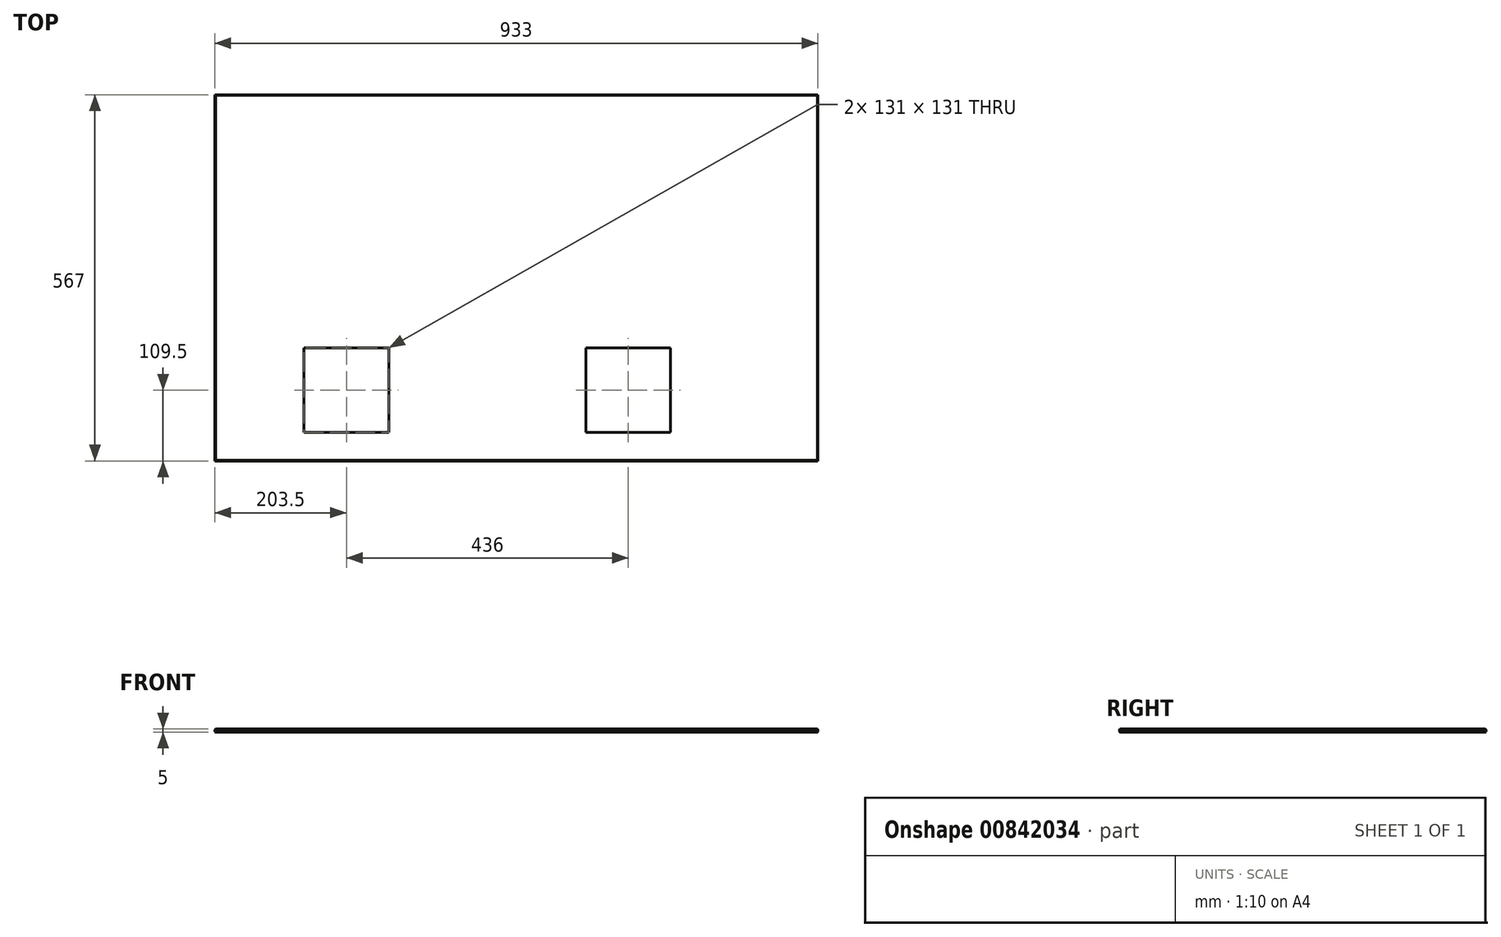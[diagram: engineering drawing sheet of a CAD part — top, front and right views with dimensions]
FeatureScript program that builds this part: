
annotation { "Feature Type Name" : "Feature", "Feature Type Description" : "" }
export const myFeature = defineFeature(function(context is Context, id is Id, definition is map)
    precondition{}
    {
        {
            var Q0;
            Q0=qCreatedBy(makeId("Top.planeOp"),FACE);
            var sketch = newSketch(context, id + "F0", { "sketchPlane" : qUnion([Q0])});
            skLineSegment(sketch, "E0.bottom", {"start": v(-466.5, 283.5) * mm, "end": v(466.5, 283.5) * mm});
            skLineSegment(sketch, "E0.top", {"start": v(-466.5, -283.5) * mm, "end": v(466.5, -283.5) * mm});
            skLineSegment(sketch, "E0.left", {"start": v(-466.5, 283.5) * mm, "end": v(-466.5, -283.5) * mm});
            skLineSegment(sketch, "E0.right", {"start": v(466.5, 283.5) * mm, "end": v(466.5, -283.5) * mm});
            skPoint(sketch, "E0.middle", {"position": v(0, 0) * mm});
            skSolve(sketch);
        }
        {
            var Q0;
            Q0=makeQuery(id+"F0.imprint","IMPRINT",FACE,{"disambiguationData":[TD([[makeQuery(id+"F0.imprint","IMPRINT",EDGE,{"derivedFrom":sQuery(id+"F0.wireOp",EDGE,"E0.bottom")}),-1.0]])]});
            extrude(context, id + "F1", {"entities" : qUnion([Q0]), "endBound" : BoundingType.SYMMETRIC, "depth" : 5 * mm, "offsetDistance" : 25 * mm});
        }
        {
            var Q0;
            Q0=makeQuery(id+"F1.opExtrude","CAP_FACE",FACE,{"disambiguationData":[OSD([sQuery(id+"F0.wireOp",EDGE,"E0.bottom"),sQuery(id+"F0.wireOp",EDGE,"E0.top"),sQuery(id+"F0.wireOp",EDGE,"E0.left"),sQuery(id+"F0.wireOp",EDGE,"E0.right")])],"isStart":false});
            var sketch = newSketch(context, id + "F2", { "sketchPlane" : qUnion([Q0])});
            skLineSegment(sketch, "E1.bottom", {"start": v(-328.5, -108.5) * mm, "end": v(-197.5, -108.5) * mm});
            skLineSegment(sketch, "E1.top", {"start": v(-328.5, -239.5) * mm, "end": v(-197.5, -239.5) * mm});
            skLineSegment(sketch, "E1.left", {"start": v(-328.5, -108.5) * mm, "end": v(-328.5, -239.5) * mm});
            skLineSegment(sketch, "E1.right", {"start": v(-197.5, -108.5) * mm, "end": v(-197.5, -239.5) * mm});
            skSolve(sketch);
        }
        {
            var Q0;
            Q0=makeQuery(id+"F2.imprint","IMPRINT",FACE,{"disambiguationData":[TD([[makeQuery(id+"F2.imprint","IMPRINT",EDGE,{"derivedFrom":sQuery(id+"F2.wireOp",EDGE,"E1.bottom")}),-1.0]])]});
            extrude(context, id + "F3", {"entities" : qUnion([Q0]), "operationType" : NewBodyOperationType.REMOVE, "endBound" : BoundingType.THROUGH_ALL, "oppositeDirection" : true, "depth" : 25 * mm, "offsetDistance" : 25 * mm});
        }
        {
            var Q0;
            Q0=makeQuery(id+"F2.imprint","IMPRINT",FACE,{"disambiguationData":[TD([[makeQuery(id+"F2.imprint","IMPRINT",EDGE,{"derivedFrom":sQuery(id+"F2.wireOp",EDGE,"E1.bottom")}),1.0]])]});
            var sketch = newSketch(context, id + "F4", { "sketchPlane" : qUnion([Q0])});
            skLineSegment(sketch, "E2.bottom", {"start": v(107.5, -108.5) * mm, "end": v(238.5, -108.5) * mm});
            skLineSegment(sketch, "E2.top", {"start": v(107.5, -239.5) * mm, "end": v(238.5, -239.5) * mm});
            skLineSegment(sketch, "E2.left", {"start": v(107.5, -108.5) * mm, "end": v(107.5, -239.5) * mm});
            skLineSegment(sketch, "E2.right", {"start": v(238.5, -108.5) * mm, "end": v(238.5, -239.5) * mm});
            skSolve(sketch);
        }
        {
            var Q0;
            Q0=makeQuery(id+"F4.imprint","IMPRINT",FACE,{"disambiguationData":[TD([[makeQuery(id+"F4.imprint","IMPRINT",EDGE,{"derivedFrom":sQuery(id+"F4.wireOp",EDGE,"E2.bottom")}),-1.0]])]});
            extrude(context, id + "F5", {"entities" : qUnion([Q0]), "operationType" : NewBodyOperationType.REMOVE, "endBound" : BoundingType.THROUGH_ALL, "oppositeDirection" : true, "depth" : 25 * mm, "offsetDistance" : 25 * mm});
        }
        {
            var Q0;
            Q0=makeQuery(id+"F1.opExtrude","CAP_EDGE",EDGE,{"disambiguationData":[OSD([sQuery(id+"F0.wireOp",EDGE,"E0.left")])],"isStart":false});
            var Q1;
            Q1=makeQuery(id+"F1.opExtrude","CAP_EDGE",EDGE,{"disambiguationData":[OSD([sQuery(id+"F0.wireOp",EDGE,"E0.left")])],"isStart":true});
            var Q2;
            Q2=makeQuery(id+"F1.opExtrude","CAP_EDGE",EDGE,{"disambiguationData":[OSD([sQuery(id+"F0.wireOp",EDGE,"E0.top")])],"isStart":true});
            var Q3;
            Q3=makeQuery(id+"F1.opExtrude","CAP_EDGE",EDGE,{"disambiguationData":[OSD([sQuery(id+"F0.wireOp",EDGE,"E0.top")])],"isStart":false});
            var Q4;
            Q4=makeQuery(id+"F1.opExtrude","CAP_EDGE",EDGE,{"disambiguationData":[OSD([sQuery(id+"F0.wireOp",EDGE,"E0.right")])],"isStart":true});
            var Q5;
            Q5=makeQuery(id+"F1.opExtrude","CAP_EDGE",EDGE,{"disambiguationData":[OSD([sQuery(id+"F0.wireOp",EDGE,"E0.right")])],"isStart":false});
            var Q6;
            Q6=makeQuery(id+"F1.opExtrude","CAP_EDGE",EDGE,{"disambiguationData":[OSD([sQuery(id+"F0.wireOp",EDGE,"E0.bottom")])],"isStart":false});
            var Q7;
            Q7=makeQuery(id+"F1.opExtrude","CAP_EDGE",EDGE,{"disambiguationData":[OSD([sQuery(id+"F0.wireOp",EDGE,"E0.bottom")])],"isStart":true});
            chamfer(context, id + "F6", {"entities" : qUnion([Q0, Q1, Q2, Q3, Q4, Q5, Q6, Q7]), "width" : 1 * mm, "tangentPropagation" : true});
        }
    });
